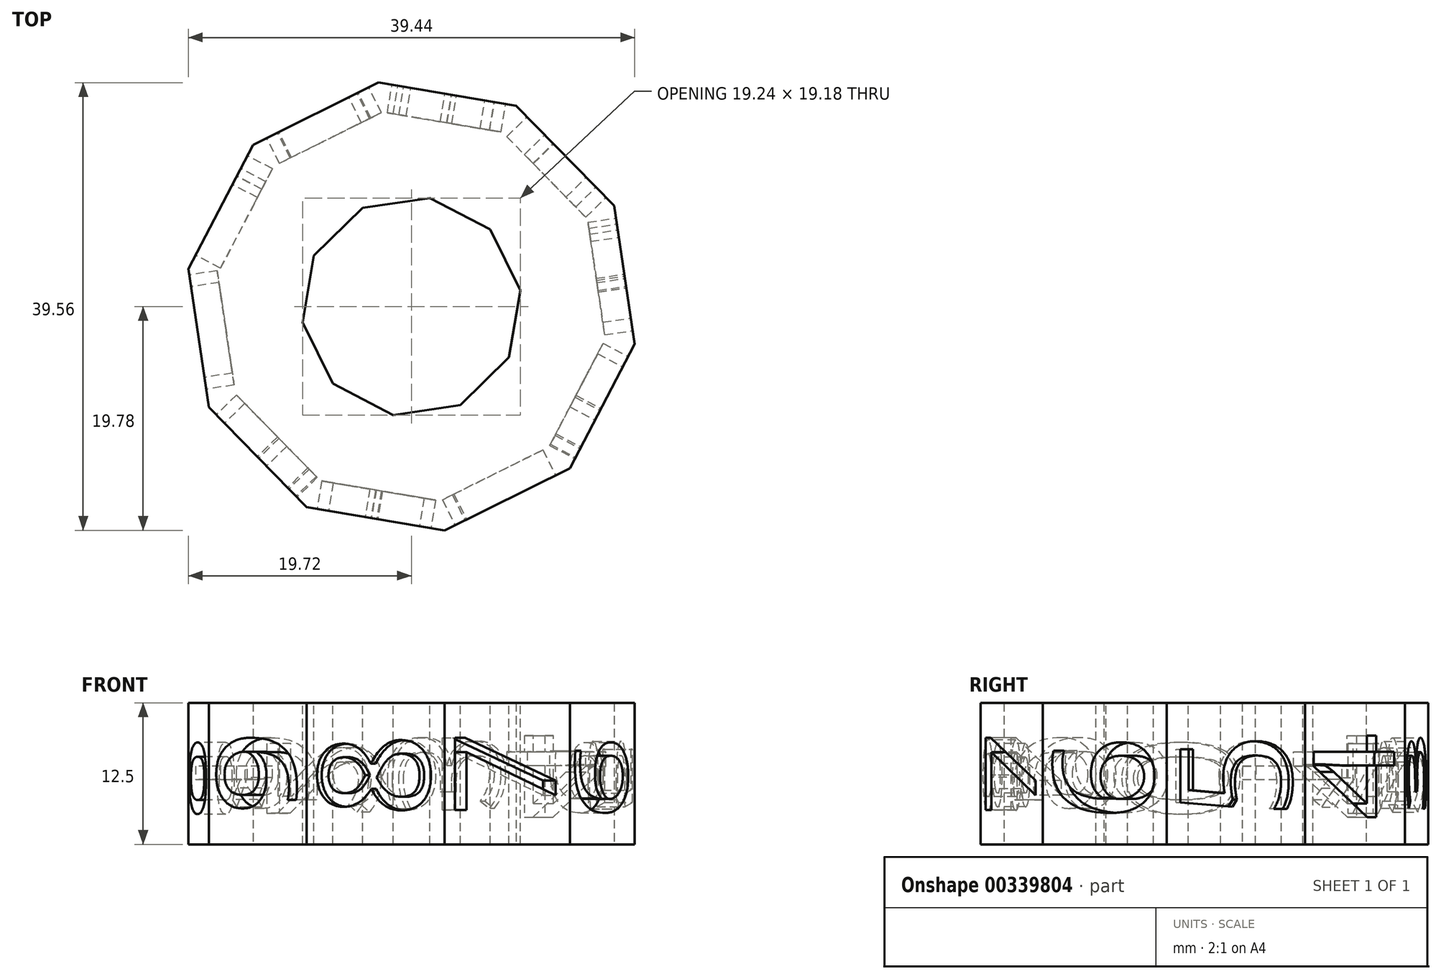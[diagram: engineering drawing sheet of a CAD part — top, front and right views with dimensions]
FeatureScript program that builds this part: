
annotation { "Feature Type Name" : "Feature", "Feature Type Description" : "" }
export const myFeature = defineFeature(function(context is Context, id is Id, definition is map)
    precondition{}
    {
        {
            var Q0;
            Q0=qCreatedBy(makeId("Top.planeOp"),FACE);
            var sketch = newSketch(context, id + "F0", { "sketchPlane" : qUnion([Q0])});
            skCircle(sketch, "E0", {"center": v(0, 0) * mm, "radius": 20 * mm});
            skCircle(sketch, "E1.cCircle", {"center": v(0, 0) * mm, "radius": 20 * mm, "construction": true});
            skLineSegment(sketch, "E1.0", {"start": v(14, -14.29) * mm, "end": v(2.93, -19.78) * mm});
            skLineSegment(sketch, "E1.1", {"start": v(2.93, -19.78) * mm, "end": v(-9.26, -17.73) * mm});
            skLineSegment(sketch, "E1.2", {"start": v(-9.26, -17.73) * mm, "end": v(-17.91, -8.9) * mm});
            skLineSegment(sketch, "E1.3", {"start": v(-17.91, -8.9) * mm, "end": v(-19.72, 3.33) * mm});
            skLineSegment(sketch, "E1.4", {"start": v(-19.72, 3.33) * mm, "end": v(-14, 14.29) * mm});
            skLineSegment(sketch, "E1.5", {"start": v(-14, 14.29) * mm, "end": v(-2.93, 19.78) * mm});
            skLineSegment(sketch, "E1.6", {"start": v(-2.93, 19.78) * mm, "end": v(9.26, 17.73) * mm});
            skLineSegment(sketch, "E1.7", {"start": v(9.26, 17.73) * mm, "end": v(17.91, 8.9) * mm});
            skLineSegment(sketch, "E1.8", {"start": v(17.91, 8.9) * mm, "end": v(19.72, -3.33) * mm});
            skLineSegment(sketch, "E1.9", {"start": v(19.72, -3.33) * mm, "end": v(14, -14.29) * mm});
            skSolve(sketch);
        }
        {
            var Q0;
            Q0=makeQuery(id+"F0.imprint","IMPRINT",FACE,{"disambiguationData":[TD([[makeQuery(id+"F0.imprint","IMPRINT",EDGE,{"derivedFrom":sQuery(id+"F0.wireOp",EDGE,"E1.0")}),-1.0]])]});
            extrude(context, id + "F1", {"entities" : qUnion([Q0]), "depth" : 12.5 * mm});
        }
        {
            var Q0;
            Q0=makeQuery(id+"F1.opExtrude","SWEPT_FACE",FACE,{"disambiguationData":[OSD([sQuery(id+"F0.wireOp",EDGE,"E1.3")])]});
            var sketch = newSketch(context, id + "F2", { "sketchPlane" : qUnion([Q0])});
            skText(sketch, "E2", { "text": "0", "fontName": "DroidSansMono.ttf"});
            const initialGuessF2  = {"E2": [-0.0055, 0.01, 0, -1, 0.01]};
            skSetInitialGuess(sketch, initialGuessF2);
            skSolve(sketch);
        }
        {
            var Q0;
            Q0 = qSketchRegion(id + "F2", true);
            extrude(context, id + "F3", {"entities" : qUnion([Q0]), "operationType" : NewBodyOperationType.REMOVE, "oppositeDirection" : true, "depth" : 2.5 * mm});
        }
        {
            var Q0;
            Q0=makeQuery(id+"F1.opExtrude","SWEPT_FACE",FACE,{"disambiguationData":[OSD([sQuery(id+"F0.wireOp",EDGE,"E1.4")])]});
            var sketch = newSketch(context, id + "F4", { "sketchPlane" : qUnion([Q0])});
            skText(sketch, "E3", { "text": "1", "fontName": "DroidSansMono.ttf"});
            const initialGuessF4  = {"E3": [0.00482, 0.00178, 0, 1, 0.01]};
            skSetInitialGuess(sketch, initialGuessF4);
            skSolve(sketch);
        }
        {
            var Q0;
            Q0 = qSketchRegion(id + "F4", true);
            extrude(context, id + "F5", {"entities" : qUnion([Q0]), "operationType" : NewBodyOperationType.REMOVE, "oppositeDirection" : true, "depth" : 2.5 * mm});
        }
        {
            var Q0;
            Q0=makeQuery(id+"F1.opExtrude","SWEPT_FACE",FACE,{"disambiguationData":[OSD([sQuery(id+"F0.wireOp",EDGE,"E1.5")])]});
            var sketch = newSketch(context, id + "F6", { "sketchPlane" : qUnion([Q0])});
            skText(sketch, "E4", { "text": "2", "fontName": "DroidSansMono.ttf"});
            const initialGuessF6  = {"E4": [0.00482, 0.00167, 0, 1, 0.01]};
            skSetInitialGuess(sketch, initialGuessF6);
            skSolve(sketch);
        }
        {
            var Q0;
            Q0 = qSketchRegion(id + "F6", true);
            extrude(context, id + "F7", {"entities" : qUnion([Q0]), "operationType" : NewBodyOperationType.REMOVE, "oppositeDirection" : true, "depth" : 2.5 * mm});
        }
        {
            var Q0;
            Q0=makeQuery(id+"F1.opExtrude","SWEPT_FACE",FACE,{"disambiguationData":[OSD([sQuery(id+"F0.wireOp",EDGE,"E1.6")])]});
            var sketch = newSketch(context, id + "F8", { "sketchPlane" : qUnion([Q0])});
            skText(sketch, "E5", { "text": "3", "fontName": "DroidSansMono.ttf"});
            const initialGuessF8  = {"E5": [0.00482, 0.00226, 0, 1, 0.01]};
            skSetInitialGuess(sketch, initialGuessF8);
            skSolve(sketch);
        }
        {
            var Q0;
            Q0 = qSketchRegion(id + "F8", true);
            extrude(context, id + "F9", {"entities" : qUnion([Q0]), "operationType" : NewBodyOperationType.REMOVE, "oppositeDirection" : true, "depth" : 2.5 * mm});
        }
        {
            var Q0;
            Q0=makeQuery(id+"F1.opExtrude","SWEPT_FACE",FACE,{"disambiguationData":[OSD([sQuery(id+"F0.wireOp",EDGE,"E1.7")])]});
            var sketch = newSketch(context, id + "F10", { "sketchPlane" : qUnion([Q0])});
            skText(sketch, "E6", { "text": "4", "fontName": "DroidSansMono.ttf"});
            const initialGuessF10  = {"E6": [0.00482, 0.00198, 0, 1, 0.01]};
            skSetInitialGuess(sketch, initialGuessF10);
            skSolve(sketch);
        }
        {
            var Q0;
            Q0 = qSketchRegion(id + "F10", true);
            extrude(context, id + "F11", {"entities" : qUnion([Q0]), "operationType" : NewBodyOperationType.REMOVE, "oppositeDirection" : true, "depth" : 2.5 * mm});
        }
        {
            var Q0;
            Q0=makeQuery(id+"F1.opExtrude","SWEPT_FACE",FACE,{"disambiguationData":[OSD([sQuery(id+"F0.wireOp",EDGE,"E1.8")])]});
            var sketch = newSketch(context, id + "F12", { "sketchPlane" : qUnion([Q0])});
            skText(sketch, "E7", { "text": "5", "fontName": "DroidSansMono.ttf"});
            const initialGuessF12  = {"E7": [0.00494, 0.00196, 0, 1, 0.01]};
            skSetInitialGuess(sketch, initialGuessF12);
            skSolve(sketch);
        }
        {
            var Q0;
            Q0 = qSketchRegion(id + "F12", true);
            extrude(context, id + "F13", {"entities" : qUnion([Q0]), "operationType" : NewBodyOperationType.REMOVE, "oppositeDirection" : true, "depth" : 2.5 * mm});
        }
        {
            var Q0;
            Q0=makeQuery(id+"F1.opExtrude","SWEPT_FACE",FACE,{"disambiguationData":[OSD([sQuery(id+"F0.wireOp",EDGE,"E1.9")])]});
            var sketch = newSketch(context, id + "F14", { "sketchPlane" : qUnion([Q0])});
            skText(sketch, "E8", { "text": "6", "fontName": "DroidSansMono.ttf"});
            const initialGuessF14  = {"E8": [0.00482, 0.00173, 0, 1, 0.01]};
            skSetInitialGuess(sketch, initialGuessF14);
            skSolve(sketch);
        }
        {
            var Q0;
            Q0 = qSketchRegion(id + "F14", true);
            extrude(context, id + "F15", {"entities" : qUnion([Q0]), "operationType" : NewBodyOperationType.REMOVE, "oppositeDirection" : true, "depth" : 2.5 * mm});
        }
        {
            var Q0;
            Q0=makeQuery(id+"F1.opExtrude","SWEPT_FACE",FACE,{"disambiguationData":[OSD([sQuery(id+"F0.wireOp",EDGE,"E1.0")])]});
            var sketch = newSketch(context, id + "F16", { "sketchPlane" : qUnion([Q0])});
            skText(sketch, "E9", { "text": "7", "fontName": "DroidSansMono.ttf"});
            const initialGuessF16  = {"E9": [0.00477, 0.00207, 0, 1, 0.01]};
            skSetInitialGuess(sketch, initialGuessF16);
            skSolve(sketch);
        }
        {
            var Q0;
            Q0 = qSketchRegion(id + "F16", true);
            extrude(context, id + "F17", {"entities" : qUnion([Q0]), "operationType" : NewBodyOperationType.REMOVE, "oppositeDirection" : true, "depth" : 2.5 * mm});
        }
        {
            var Q0;
            Q0=makeQuery(id+"F1.opExtrude","SWEPT_FACE",FACE,{"disambiguationData":[OSD([sQuery(id+"F0.wireOp",EDGE,"E1.1")])]});
            var sketch = newSketch(context, id + "F18", { "sketchPlane" : qUnion([Q0])});
            skText(sketch, "E10", { "text": "8", "fontName": "DroidSansMono.ttf"});
            const initialGuessF18  = {"E10": [0.00482, 0.00194, 0, 1, 0.01]};
            skSetInitialGuess(sketch, initialGuessF18);
            skSolve(sketch);
        }
        {
            var Q0;
            Q0 = qSketchRegion(id + "F18", true);
            extrude(context, id + "F19", {"entities" : qUnion([Q0]), "operationType" : NewBodyOperationType.REMOVE, "oppositeDirection" : true, "depth" : 2.5 * mm});
        }
        {
            var Q0;
            Q0=makeQuery(id+"F1.opExtrude","SWEPT_FACE",FACE,{"disambiguationData":[OSD([sQuery(id+"F0.wireOp",EDGE,"E1.2")])]});
            var sketch = newSketch(context, id + "F20", { "sketchPlane" : qUnion([Q0])});
            skText(sketch, "E11", { "text": "9", "fontName": "DroidSansMono.ttf"});
            const initialGuessF20  = {"E11": [0.00482, 0.00213, 0, 1, 0.01]};
            skSetInitialGuess(sketch, initialGuessF20);
            skSolve(sketch);
        }
        {
            var Q0;
            Q0 = qSketchRegion(id + "F20", true);
            extrude(context, id + "F21", {"entities" : qUnion([Q0]), "operationType" : NewBodyOperationType.REMOVE, "oppositeDirection" : true, "depth" : 2.5 * mm});
        }
        {
            var Q0;
            Q0=makeQuery(id+"F1.opExtrude","CAP_FACE",FACE,{"disambiguationData":[OSD([sQuery(id+"F0.wireOp",EDGE,"E1.0"),sQuery(id+"F0.wireOp",EDGE,"E1.1"),sQuery(id+"F0.wireOp",EDGE,"E1.2"),sQuery(id+"F0.wireOp",EDGE,"E1.3"),sQuery(id+"F0.wireOp",EDGE,"E1.4"),sQuery(id+"F0.wireOp",EDGE,"E1.5"),sQuery(id+"F0.wireOp",EDGE,"E1.6"),sQuery(id+"F0.wireOp",EDGE,"E1.7"),sQuery(id+"F0.wireOp",EDGE,"E1.8"),sQuery(id+"F0.wireOp",EDGE,"E1.9")])],"isStart":false});
            var sketch = newSketch(context, id + "F22", { "sketchPlane" : qUnion([Q0])});
            skCircle(sketch, "E12", {"center": v(0, 0) * mm, "radius": 9.25 * mm});
            skLineSegment(sketch, "E13", {"start": v(-2.93, 19.78) * mm, "end": v(2.93, -19.78) * mm});
            skCircle(sketch, "E14.cCircle", {"center": v(0, 0) * mm, "radius": 9.25 * mm, "construction": true});
            skLineSegment(sketch, "E14.0", {"start": v(4.33, -8.71) * mm, "end": v(-1.62, -9.6) * mm});
            skLineSegment(sketch, "E14.1", {"start": v(-1.62, -9.6) * mm, "end": v(-6.95, -6.8) * mm});
            skLineSegment(sketch, "E14.2", {"start": v(-6.95, -6.8) * mm, "end": v(-9.62, -1.42) * mm});
            skLineSegment(sketch, "E14.3", {"start": v(-9.62, -1.42) * mm, "end": v(-8.62, 4.5) * mm});
            skLineSegment(sketch, "E14.4", {"start": v(-8.62, 4.5) * mm, "end": v(-4.33, 8.71) * mm});
            skLineSegment(sketch, "E14.5", {"start": v(-4.33, 8.71) * mm, "end": v(1.62, 9.6) * mm});
            skLineSegment(sketch, "E14.6", {"start": v(1.62, 9.6) * mm, "end": v(6.95, 6.8) * mm});
            skLineSegment(sketch, "E14.7", {"start": v(6.95, 6.8) * mm, "end": v(9.62, 1.42) * mm});
            skLineSegment(sketch, "E14.8", {"start": v(9.62, 1.42) * mm, "end": v(8.62, -4.5) * mm});
            skLineSegment(sketch, "E14.9", {"start": v(8.62, -4.5) * mm, "end": v(4.33, -8.71) * mm});
            skPoint(sketch, "E14.0.midPoint", {"position": v(1.35, -9.15) * mm});
            skSolve(sketch);
        }
        {
            var Q0;
            Q0 = qSketchRegion(id + "F22", true);
            extrude(context, id + "F23", {"entities" : qUnion([Q0]), "operationType" : NewBodyOperationType.REMOVE, "oppositeDirection" : true, "depth" : 25 * mm});
        }
    });
